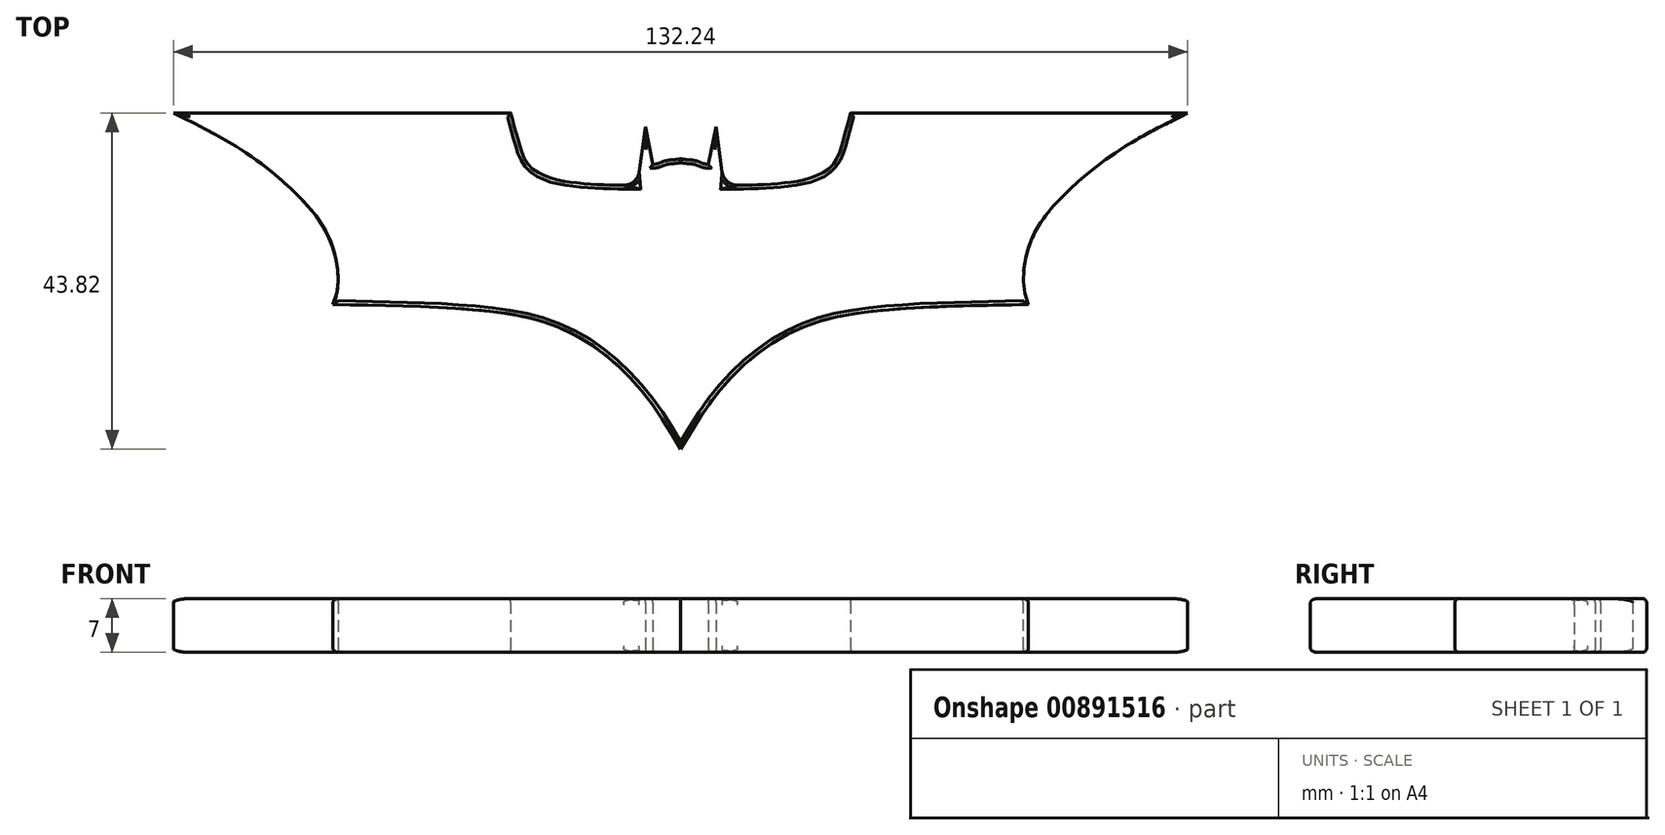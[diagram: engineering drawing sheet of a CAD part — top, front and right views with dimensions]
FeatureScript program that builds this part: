
annotation { "Feature Type Name" : "Feature", "Feature Type Description" : "" }
export const myFeature = defineFeature(function(context is Context, id is Id, definition is map)
    precondition{}
    {
        {
            var Q0;
            Q0=qCreatedBy(makeId("Top.planeOp"),FACE);
            var sketch = newSketch(context, id + "F0", { "sketchPlane" : qUnion([Q0])});
            skFitSpline(sketch, "E0", {"points": [v(66.12, 14.99) * mm, v(56.4, 9.6) * mm, v(47.88, 1.98) * mm, v(45.03, -3.7) * mm, v(45.33, -9.99) * mm], "startDerivative": vector(-34.46, -16.89) * mm, "endDerivative": vector(12.6, -27.31) * mm});
            skFitSpline(sketch, "E1", {"points": [v(0, -28.83) * mm, v(5.85, -20.3) * mm, v(14.82, -13.43) * mm, v(26.2, -10.73) * mm, v(45.33, -9.99) * mm], "startDerivative": vector(23.38, 39.27) * mm, "endDerivative": vector(66.84, 1.08) * mm});
            skLineSegment(sketch, "E2", {"start": v(66.12, 14.99) * mm, "end": v(22.15, 14.99) * mm});
            skFitSpline(sketch, "E3", {"points": [v(22.15, 14.99) * mm, v(21.12, 11.16) * mm, v(19.74, 8.13) * mm, v(15.72, 6.2) * mm, v(5.65, 5.55) * mm], "startDerivative": vector(-4.7, -17.78) * mm, "endDerivative": vector(-31.64, -0.41) * mm});
            skLineSegment(sketch, "E4", {"start": v(4.6, 13.2) * mm, "end": v(5.65, 5.55) * mm});
            skLineSegment(sketch, "E5", {"start": v(4.6, 13.2) * mm, "end": v(3.6, 8.3) * mm});
            skFitSpline(sketch, "E6", {"points": [v(3.6, 8.3) * mm, v(1.9, 8.78) * mm, v(0, 9.01) * mm], "startDerivative": vector(-4.72, 0) * mm, "endDerivative": vector(-3.6, 0.88) * mm});
            skFitSpline(sketch, "E7.MirrorCS", {"points": [v(-3.6, 8.3) * mm, v(-1.9, 8.78) * mm, v(0, 9.01) * mm], "startDerivative": vector(4.72, 0) * mm, "endDerivative": vector(3.6, 0.88) * mm});
            skLineSegment(sketch, "E8.MirrorCS", {"start": v(-4.6, 13.2) * mm, "end": v(-3.6, 8.3) * mm});
            skLineSegment(sketch, "E9.MirrorCS", {"start": v(-66.12, 14.99) * mm, "end": v(-22.15, 14.99) * mm});
            skLineSegment(sketch, "E10.MirrorCS", {"start": v(-4.6, 13.2) * mm, "end": v(-5.65, 5.55) * mm});
            skFitSpline(sketch, "E11.MirrorCS", {"points": [v(-22.15, 14.99) * mm, v(-21.12, 11.16) * mm, v(-19.74, 8.13) * mm, v(-15.72, 6.2) * mm, v(-5.65, 5.55) * mm], "startDerivative": vector(4.7, -17.78) * mm, "endDerivative": vector(31.64, -0.41) * mm});
            skFitSpline(sketch, "E12.MirrorCS", {"points": [v(-66.12, 14.99) * mm, v(-56.4, 9.6) * mm, v(-47.88, 1.98) * mm, v(-45.03, -3.7) * mm, v(-45.33, -9.99) * mm], "startDerivative": vector(34.46, -16.89) * mm, "endDerivative": vector(-12.6, -27.31) * mm});
            skFitSpline(sketch, "E13.MirrorCS", {"points": [v(0, -28.83) * mm, v(-5.85, -20.3) * mm, v(-14.82, -13.43) * mm, v(-26.2, -10.73) * mm, v(-45.33, -9.99) * mm], "startDerivative": vector(-23.38, 39.27) * mm, "endDerivative": vector(-66.84, 1.08) * mm});
            skPoint(sketch, "E14", {"position": v(-45.33, 14.99) * mm});
            skSolve(sketch);
        }
        {
            var Q0;
            Q0=makeQuery(id+"F0.imprint","IMPRINT",FACE,{"disambiguationData":[TD([[makeQuery(id+"F0.imprint","IMPRINT",EDGE,{"derivedFrom":sQuery(id+"F0.wireOp",EDGE,"u5Xsr1R6-GVs2-ksxk-sBhS-9xSzsXB6sLCF")}),-1.0]])]});
            var Q1;
            Q1=makeQuery(id+"F0.imprint","IMPRINT",FACE,{"disambiguationData":[TD([[makeQuery(id+"F0.imprint","IMPRINT",EDGE,{"derivedFrom":sQuery(id+"F0.wireOp",EDGE,"E0")}),-1.0]])]});
            extrude(context, id + "F1", {"entities" : qUnion([Q0, Q1]), "depth" : 7 * mm, "offsetDistance" : 25 * mm});
        }
        {
            var Q0;
            Q0=makeQuery(id+"F1.opExtrude","CAP_FACE",FACE,{"disambiguationData":[OSD([sQuery(id+"F0.wireOp",EDGE,"u5Xsr1R6-GVs2-ksxk-sBhS-9xSzsXB6sLCF"),sQuery(id+"F0.wireOp",EDGE,"E0"),sQuery(id+"F0.wireOp",EDGE,"E1"),sQuery(id+"F0.wireOp",EDGE,"E2"),sQuery(id+"F0.wireOp",EDGE,"E3"),sQuery(id+"F0.wireOp",EDGE,"E4"),sQuery(id+"F0.wireOp",EDGE,"E5"),sQuery(id+"F0.wireOp",EDGE,"E6"),sQuery(id+"F0.wireOp",EDGE,"E7.MirrorCS"),sQuery(id+"F0.wireOp",EDGE,"E8.MirrorCS"),sQuery(id+"F0.wireOp",EDGE,"E9.MirrorCS"),sQuery(id+"F0.wireOp",EDGE,"E10.MirrorCS"),sQuery(id+"F0.wireOp",EDGE,"E11.MirrorCS"),sQuery(id+"F0.wireOp",EDGE,"e1f9da1c-24f0-4bde-bbed-4b3cddc4433e5.MirrorC"),sQuery(id+"F0.wireOp",EDGE,"E12.MirrorCS"),sQuery(id+"F0.wireOp",EDGE,"E13.MirrorCS"),sQuery(id+"F0.wireOp",EDGE,"e1f9da1c-24f0-4bde-bbed-4b3cddc4433e8.MirrorC")])],"isStart":false});
            fillet(context, id + "F2", {"entities" : qUnion([Q0]), "radius" : .5 * mm, "tangentPropagation" : true, "allowEdgeOverflow" : false});
        }
        {
            var Q0;
            Q0=makeQuery(id+"F1.opExtrude","CAP_FACE",FACE,{"disambiguationData":[OSD([sQuery(id+"F0.wireOp",EDGE,"u5Xsr1R6-GVs2-ksxk-sBhS-9xSzsXB6sLCF"),sQuery(id+"F0.wireOp",EDGE,"E0"),sQuery(id+"F0.wireOp",EDGE,"E1"),sQuery(id+"F0.wireOp",EDGE,"E2"),sQuery(id+"F0.wireOp",EDGE,"E3"),sQuery(id+"F0.wireOp",EDGE,"E4"),sQuery(id+"F0.wireOp",EDGE,"E5"),sQuery(id+"F0.wireOp",EDGE,"E6"),sQuery(id+"F0.wireOp",EDGE,"E7.MirrorCS"),sQuery(id+"F0.wireOp",EDGE,"E8.MirrorCS"),sQuery(id+"F0.wireOp",EDGE,"E9.MirrorCS"),sQuery(id+"F0.wireOp",EDGE,"E10.MirrorCS"),sQuery(id+"F0.wireOp",EDGE,"E11.MirrorCS"),sQuery(id+"F0.wireOp",EDGE,"e1f9da1c-24f0-4bde-bbed-4b3cddc4433e5.MirrorC"),sQuery(id+"F0.wireOp",EDGE,"E12.MirrorCS"),sQuery(id+"F0.wireOp",EDGE,"E13.MirrorCS"),sQuery(id+"F0.wireOp",EDGE,"e1f9da1c-24f0-4bde-bbed-4b3cddc4433e8.MirrorC")])],"isStart":true});
            fillet(context, id + "F3", {"entities" : qUnion([Q0]), "radius" : .5 * mm, "tangentPropagation" : true, "allowEdgeOverflow" : false});
        }
        {
            var Q0;
            Q0=makeQuery(id+"F1.opExtrude","SWEPT_EDGE",EDGE,{"disambiguationData":[OSD([sQuery(id+"F0.wireOp",EDGE,"E3"),sQuery(id+"F0.wireOp",EDGE,"E4")])]});
            var Q1;
            Q1=makeQuery(id+"F1.opExtrude","SWEPT_EDGE",EDGE,{"disambiguationData":[OSD([sQuery(id+"F0.wireOp",EDGE,"E10.MirrorCS"),sQuery(id+"F0.wireOp",EDGE,"E11.MirrorCS")])]});
            fillet(context, id + "F4", {"entities" : qUnion([Q0, Q1]), "radius" : 2 * mm, "tangentPropagation" : true, "allowEdgeOverflow" : false});
        }
    });
